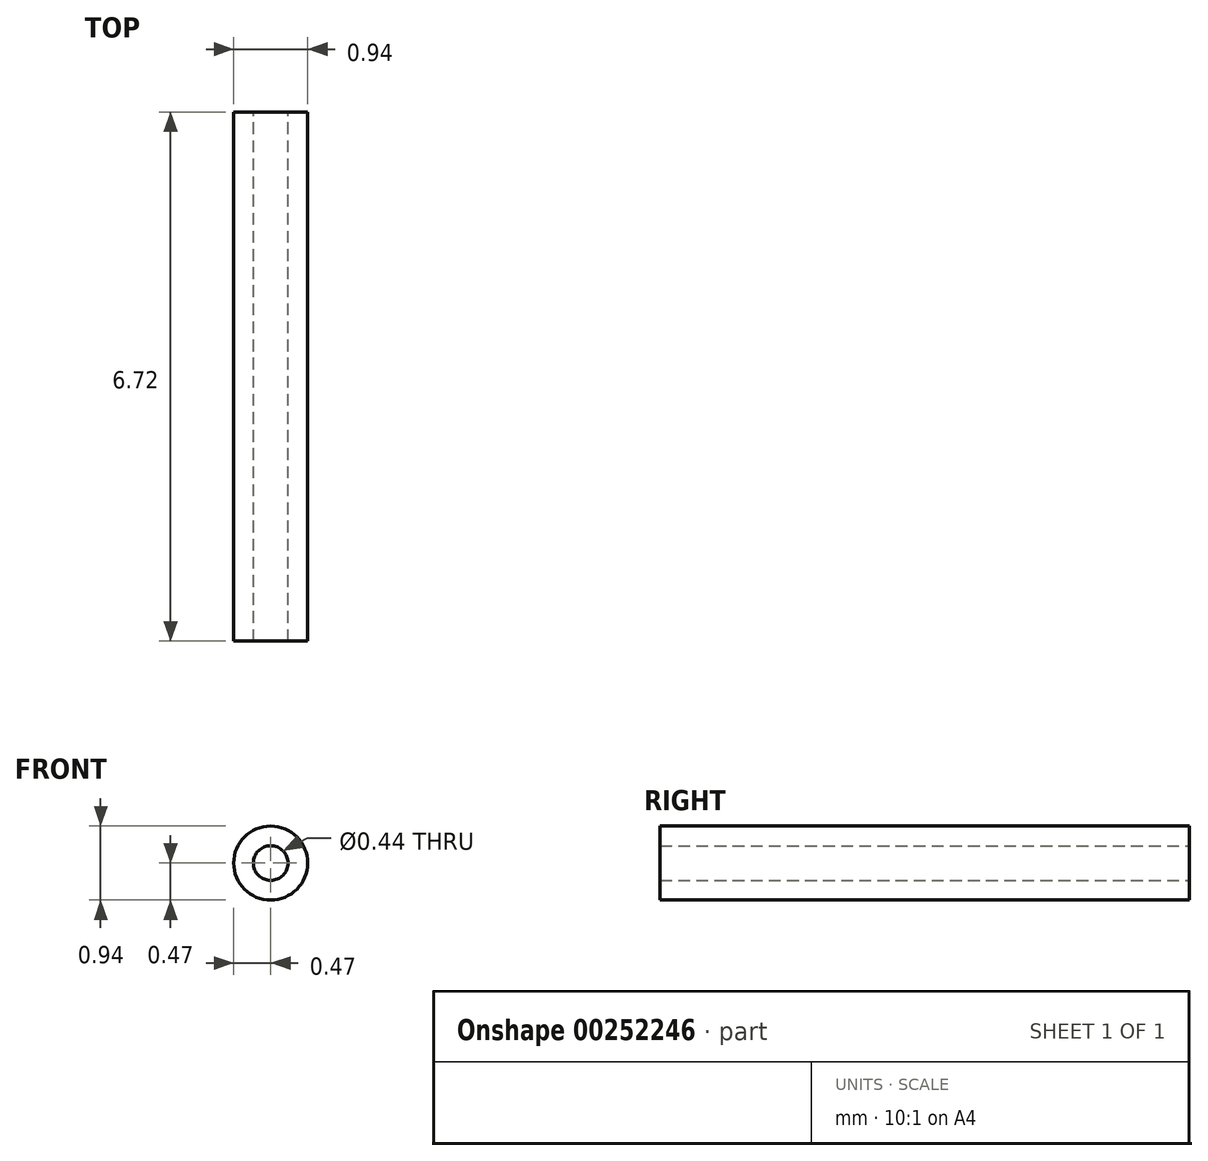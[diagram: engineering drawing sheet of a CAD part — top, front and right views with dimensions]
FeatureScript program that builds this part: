
annotation { "Feature Type Name" : "Feature", "Feature Type Description" : "" }
export const myFeature = defineFeature(function(context is Context, id is Id, definition is map)
    precondition{}
    {
        {
            var Q0;
            Q0=qCreatedBy(makeId("Front.planeOp"),FACE);
            var sketch = newSketch(context, id + "F0", { "sketchPlane" : qUnion([Q0])});
            skCircle(sketch, "E0", {"center": v(0, 0) * mm, "radius": 0.47 * mm});
            skCircle(sketch, "E1", {"center": v(0, 0) * mm, "radius": 0.22 * mm});
            skSolve(sketch);
        }
        {
            var Q0;
            Q0 = qSketchRegion(id + "F0", true);
            extrude(context, id + "F1", {"entities" : qUnion([Q0]), "depth" : 6.72 * mm});
        }
    });
